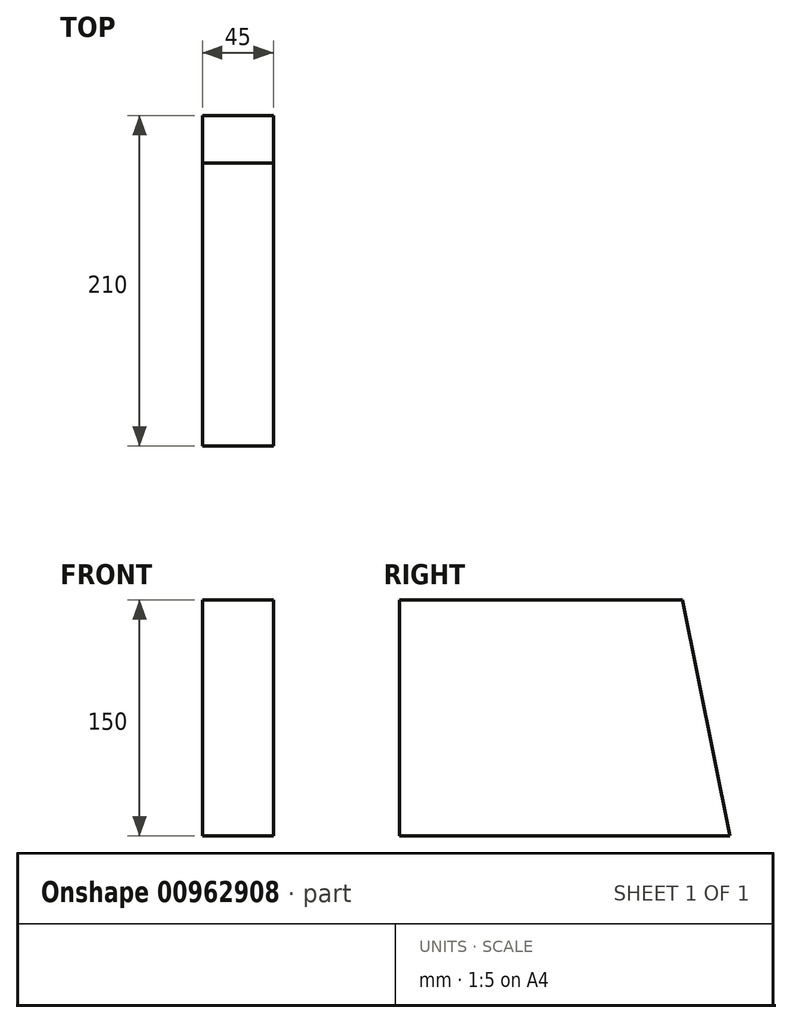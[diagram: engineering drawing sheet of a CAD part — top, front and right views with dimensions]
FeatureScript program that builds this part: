
annotation { "Feature Type Name" : "Feature", "Feature Type Description" : "" }
export const myFeature = defineFeature(function(context is Context, id is Id, definition is map)
    precondition{}
    {
        {
            var Q0;
            Q0=qCreatedBy(makeId("Right.planeOp"),FACE);
            var sketch = newSketch(context, id + "F0", { "sketchPlane" : qUnion([Q0])});
            skLineSegment(sketch, "E0.bottom", {"start": v(105, 75) * mm, "end": v(-105, 75) * mm});
            skLineSegment(sketch, "E0.top", {"start": v(105, -75) * mm, "end": v(-105, -75) * mm});
            skLineSegment(sketch, "E0.left", {"start": v(105, 75) * mm, "end": v(105, -75) * mm});
            skLineSegment(sketch, "E0.right", {"start": v(-105, 75) * mm, "end": v(-105, -75) * mm});
            skPoint(sketch, "E0.middle", {"position": v(0, 0) * mm});
            skSolve(sketch);
        }
        {
            var Q0;
            Q0 = qSketchRegion(id + "F0", true);
            extrude(context, id + "F1", {"entities" : qUnion([Q0]), "depth" : 45 * mm, "offsetDistance" : 25 * mm});
        }
        {
            var Q0;
            Q0=makeQuery(id+"F1.opExtrude","CAP_FACE",FACE,{"disambiguationData":[OSD([sQuery(id+"F0.wireOp",EDGE,"E0.bottom"),sQuery(id+"F0.wireOp",EDGE,"E0.top"),sQuery(id+"F0.wireOp",EDGE,"E0.left"),sQuery(id+"F0.wireOp",EDGE,"E0.right")])],"isStart":true});
            var sketch = newSketch(context, id + "F2", { "sketchPlane" : qUnion([Q0])});
            skLineSegment(sketch, "E1", {"start": v(105, 75) * mm, "end": v(-75, 75) * mm});
            skLineSegment(sketch, "E2", {"start": v(-75, 75) * mm, "end": v(-105, -75) * mm});
            skSolve(sketch);
        }
        {
            var Q0;
            {var subQ0=sQuery(id+"F2.wireOp",EDGE,"E2");Q0=makeQuery(id+"F2.imprint","IMPRINT",FACE,{"disambiguationData":[TD([[makeQuery(id+"F2.imprint","IMPRINT",EDGE,{"derivedFrom":subQ0}),-1.0]])]});}
            extrude(context, id + "F3", {"entities" : qUnion([Q0]), "operationType" : NewBodyOperationType.REMOVE, "oppositeDirection" : true, "depth" : 83.7 * mm, "offsetDistance" : 25 * mm});
        }
    });
